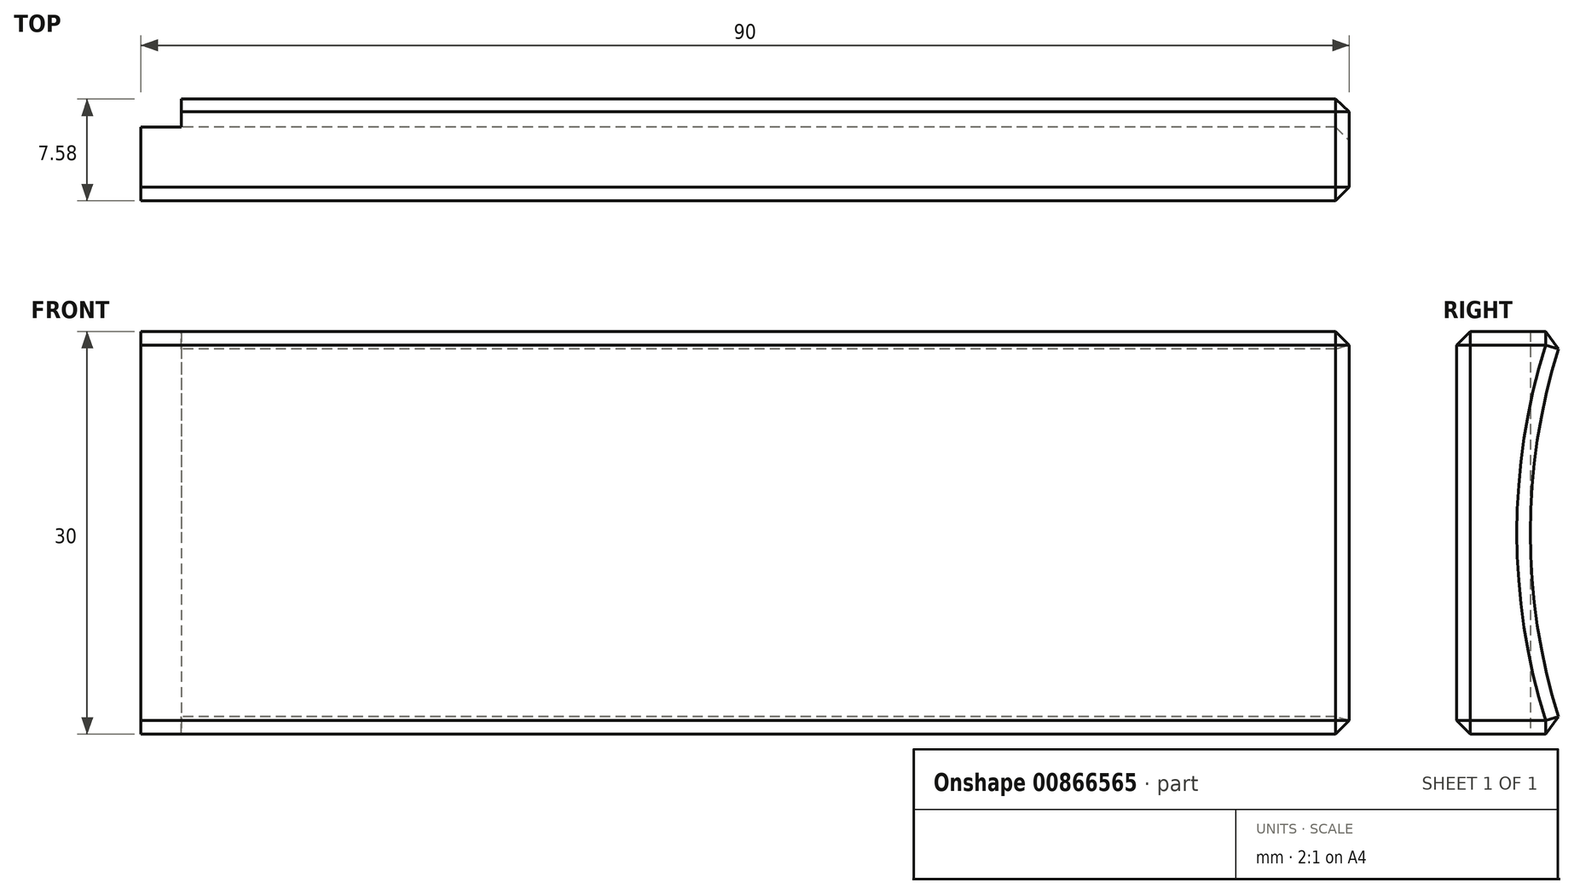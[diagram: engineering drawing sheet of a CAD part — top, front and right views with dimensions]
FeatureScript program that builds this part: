
annotation { "Feature Type Name" : "Feature", "Feature Type Description" : "" }
export const myFeature = defineFeature(function(context is Context, id is Id, definition is map)
    precondition{}
    {
        {
            var Q0;
            Q0=qCreatedBy(makeId("Right.planeOp"),FACE);
            var sketch = newSketch(context, id + "F0", { "sketchPlane" : qUnion([Q0])});
            skArc(sketch, "E0", {"start": v(-43.49, 15) * mm, "mid": v(-46, 0) * mm, "end": v(-43.49, -15) * mm});
            skLineSegment(sketch, "E1", {"start": v(-66.98, 0) * mm, "end": v(71.17, 0) * mm, "construction": true});
            skLineSegment(sketch, "E2", {"start": v(-43.49, 15) * mm, "end": v(-51.49, 15) * mm});
            skLineSegment(sketch, "E3.MirrorCS", {"start": v(-43.49, -15) * mm, "end": v(-51.49, -15) * mm});
            skLineSegment(sketch, "E4", {"start": v(-46, 0) * mm, "end": v(-46, 15) * mm});
            skLineSegment(sketch, "E5.MirrorCS", {"start": v(-46, 0) * mm, "end": v(-46, -15) * mm});
            skLineSegment(sketch, "E6", {"start": v(-51.49, 15) * mm, "end": v(-51.49, -15) * mm});
            skSolve(sketch);
        }
        {
            var Q0;
            {var subQ1=sQuery(id+"F0.wireOp",EDGE,"E4");Q0=makeQuery(id+"F0.imprint","IMPRINT",FACE,{"disambiguationData":[TD([[makeQuery(id+"F0.imprint","IMPRINT",EDGE,{"derivedFrom":subQ1}),1.0]])]});}
            extrude(context, id + "F1", {"entities" : qUnion([Q0]), "depth" : 3 * mm, "offsetDistance" : 25 * mm});
        }
        {
            var Q0;
            {var subQ1=sQuery(id+"F0.wireOp",EDGE,"E4");Q0=makeQuery(id+"F0.imprint","IMPRINT",FACE,{"disambiguationData":[TD([[makeQuery(id+"F0.imprint","IMPRINT",EDGE,{"derivedFrom":subQ1}),1.0]])]});}
            var Q1;
            {var subQ3=sQuery(id+"F0.wireOp",EDGE,"E5.MirrorCS");Q1=makeQuery(id+"F0.imprint","IMPRINT",FACE,{"disambiguationData":[TD([[makeQuery(id+"F0.imprint","IMPRINT",EDGE,{"derivedFrom":subQ3}),1.0]])]});}
            var Q2;
            {var subQ3=sQuery(id+"F0.wireOp",EDGE,"E4");Q2=makeQuery(id+"F0.imprint","IMPRINT",FACE,{"disambiguationData":[TD([[makeQuery(id+"F0.imprint","IMPRINT",EDGE,{"derivedFrom":subQ3}),-1.0]])]});}
            extrude(context, id + "F2", {"entities" : qUnion([Q0, Q1, Q2]), "operationType" : NewBodyOperationType.ADD, "depth" : 90 * mm, "offsetDistance" : 25 * mm, "hasSecondDirection" : true, "secondDirectionOppositeDirection" : false, "secondDirectionDepth" : 3 * mm});
        }
        {
            var Q0;
            Q0=makeQuery(id+"F2.opExtrude","CAP_FACE",FACE,{"disambiguationData":[OSD([sQuery(id+"F0.wireOp",EDGE,"E0"),sQuery(id+"F0.wireOp",EDGE,"E2"),sQuery(id+"F0.wireOp",EDGE,"E3.MirrorCS"),sQuery(id+"F0.wireOp",EDGE,"E6")])],"isStart":false});
            var Q1;
            Q1=makeQuery(id+"F2.opExtrude","SWEPT_EDGE",EDGE,{"disambiguationData":[OSD([sQuery(id+"F0.wireOp",EDGE,"E0"),sQuery(id+"F0.wireOp",EDGE,"E3.MirrorCS")])]});
            var Q2;
            {var subQ0=sQuery(id+"F0.wireOp",EDGE,"E6");var subQ1=sQuery(id+"F0.wireOp",EDGE,"e35a9b8b-e33d-49d9-b224-8438f97776ac0.MirrorCS");var subQ2=sQuery(id+"F0.wireOp",EDGE,"E3.MirrorCS");Q2=makeQuery(id+"F2.boolean.opBoolean","MERGE",EDGE,{"derivedFrom":[makeQuery(id+"F1.opExtrude","SWEPT_EDGE",EDGE,{"disambiguationData":[OSD([subQ2,subQ1,subQ0])]}),makeQuery(id+"F2.opExtrude","SWEPT_EDGE",EDGE,{"disambiguationData":[OSD([subQ2,subQ1,subQ0])]})]});}
            var Q3;
            Q3=makeQuery(id+"F2.opExtrude","SWEPT_EDGE",EDGE,{"disambiguationData":[OSD([sQuery(id+"F0.wireOp",EDGE,"E0"),sQuery(id+"F0.wireOp",EDGE,"E2")])]});
            var Q4;
            {var subQ0=sQuery(id+"F0.wireOp",EDGE,"E6");var subQ1=sQuery(id+"F0.wireOp",EDGE,"jXne8i6v-9Jhb-n38T-pHkT-OmubA6bHbnSs");var subQ2=sQuery(id+"F0.wireOp",EDGE,"E2");Q4=makeQuery(id+"F2.boolean.opBoolean","MERGE",EDGE,{"derivedFrom":[makeQuery(id+"F1.opExtrude","SWEPT_EDGE",EDGE,{"disambiguationData":[OSD([subQ2,subQ1,subQ0])]}),makeQuery(id+"F2.opExtrude","SWEPT_EDGE",EDGE,{"disambiguationData":[OSD([subQ2,subQ1,subQ0])]})]});}
            chamfer(context, id + "F3", {"entities" : qUnion([Q0, Q1, Q2, Q3, Q4]), "width" : 1 * mm, "tangentPropagation" : true});
        }
    });
